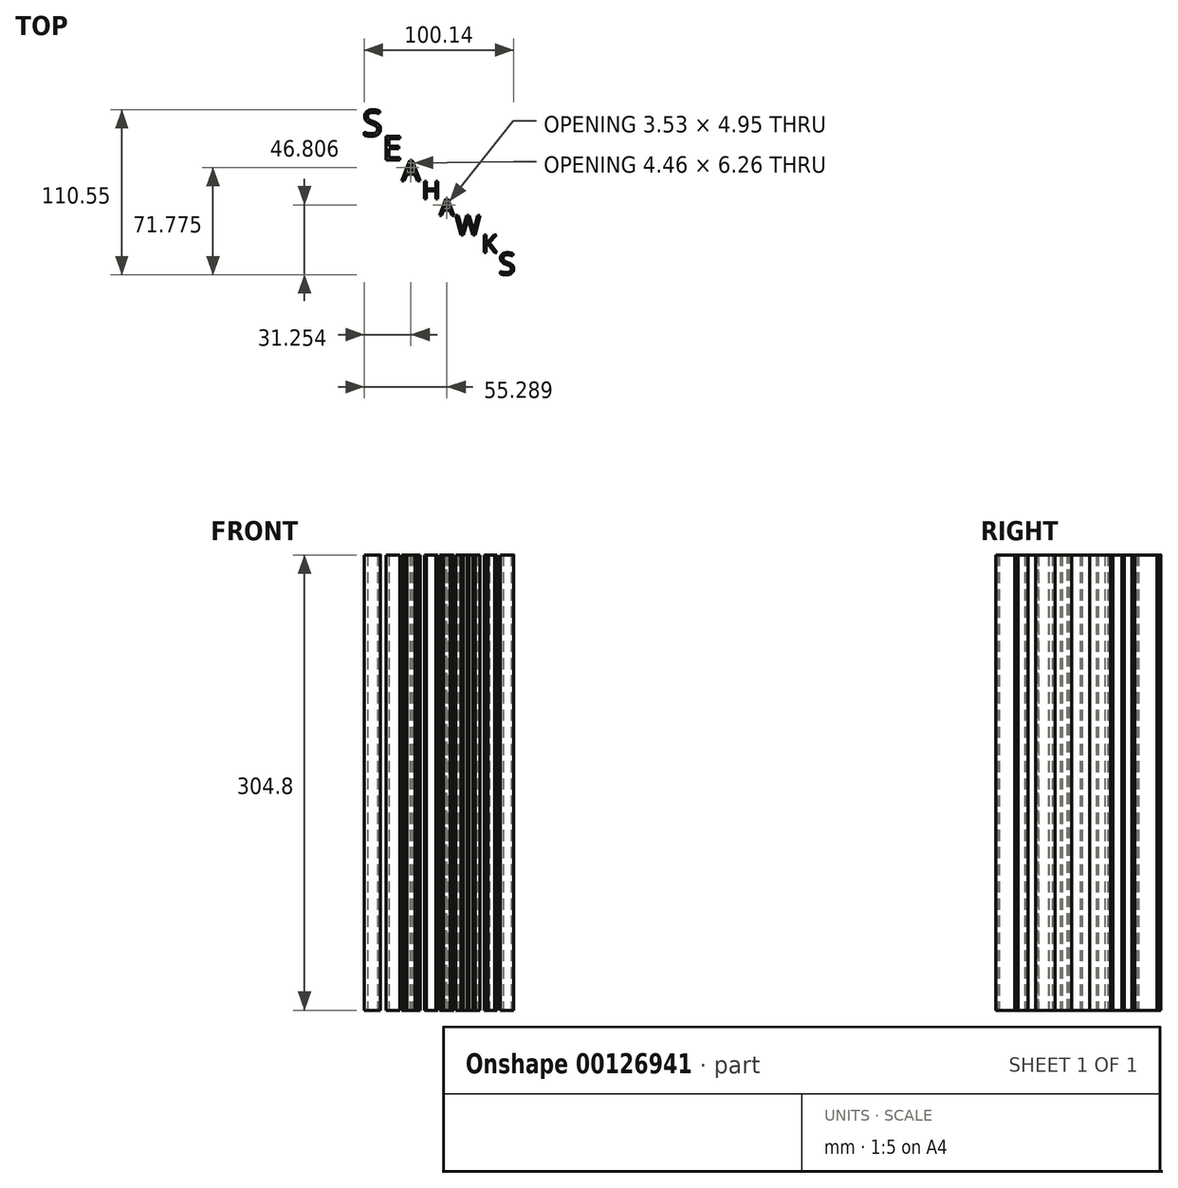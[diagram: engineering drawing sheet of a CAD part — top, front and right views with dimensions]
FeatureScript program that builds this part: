
annotation { "Feature Type Name" : "Feature", "Feature Type Description" : "" }
export const myFeature = defineFeature(function(context is Context, id is Id, definition is map)
    precondition{}
    {
        {
            var Q0;
            Q0=qCreatedBy(makeId("Top.planeOp"),FACE);
            var sketch = newSketch(context, id + "F0", { "sketchPlane" : qUnion([Q0])});
            skText(sketch, "E0", { "text": "S", "fontName": "OpenSans-Regular.ttf"});
            skText(sketch, "E1", { "text": "E", "fontName": "OpenSans-Regular.ttf"});
            skText(sketch, "E2", { "text": "A", "fontName": "OpenSans-Regular.ttf"});
            skText(sketch, "E3", { "text": "H", "fontName": "OpenSans-Regular.ttf"});
            skText(sketch, "E4", { "text": "A", "fontName": "OpenSans-Regular.ttf"});
            skText(sketch, "E5", { "text": "W", "fontName": "OpenSans-Regular.ttf"});
            skText(sketch, "E6", { "text": "K", "fontName": "OpenSans-Regular.ttf"});
            skText(sketch, "E7", { "text": "S", "fontName": "OpenSans-Regular.ttf"});
            const initialGuessF0  = {"E0": [-0.096, 0.07813, 1, 0, 0.0175], "E1": [-0.08224, 0.0619, 1, 0, 0.01624], "E2": [-0.0696, 0.048, 1, 0, 0.0139], "E3": [-0.05613, 0.0359, 1, 0, 0.01209], "E4": [-0.04429, 0.0249, 1, 0, 0.011], "E5": [-0.03362, 0.0119, 1, 0, 0.013], "E6": [-0.016, 0, 1, 0, 0.0119], "E7": [-0.00477, -0.01462, 1, 0, 0.01462]};
            skSetInitialGuess(sketch, initialGuessF0);
            skSolve(sketch);
        }
        {
            var Q0;
            Q0=makeQuery(id+"F0.imprint","IMPRINT",FACE,{"disambiguationData":[TD([[makeQuery(id+"F0.imprint","IMPRINT",EDGE,{"derivedFrom":sQuery(id+"F0.wireOp",EDGE,"E0.sketch_text.stroke-0")}),-1.0]])]});
            var Q1;
            Q1=makeQuery(id+"F0.imprint","IMPRINT",FACE,{"disambiguationData":[TD([[makeQuery(id+"F0.imprint","IMPRINT",EDGE,{"derivedFrom":sQuery(id+"F0.wireOp",EDGE,"E1.sketch_text.stroke-0")}),-1.0]])]});
            var Q2;
            Q2=makeQuery(id+"F0.imprint","IMPRINT",FACE,{"disambiguationData":[TD([[makeQuery(id+"F0.imprint","IMPRINT",EDGE,{"derivedFrom":sQuery(id+"F0.wireOp",EDGE,"E2.sketch_text.stroke-0")}),-1.0]])]});
            var Q3;
            Q3=makeQuery(id+"F0.imprint","IMPRINT",FACE,{"disambiguationData":[TD([[makeQuery(id+"F0.imprint","IMPRINT",EDGE,{"derivedFrom":sQuery(id+"F0.wireOp",EDGE,"E3.sketch_text.stroke-0")}),-1.0]])]});
            var Q4;
            Q4=makeQuery(id+"F0.imprint","IMPRINT",FACE,{"disambiguationData":[TD([[makeQuery(id+"F0.imprint","IMPRINT",EDGE,{"derivedFrom":sQuery(id+"F0.wireOp",EDGE,"E4.sketch_text.stroke-0")}),-1.0]])]});
            var Q5;
            Q5=makeQuery(id+"F0.imprint","IMPRINT",FACE,{"disambiguationData":[TD([[makeQuery(id+"F0.imprint","IMPRINT",EDGE,{"derivedFrom":sQuery(id+"F0.wireOp",EDGE,"E5.sketch_text.stroke-0")}),-1.0]])]});
            var Q6;
            Q6=makeQuery(id+"F0.imprint","IMPRINT",FACE,{"disambiguationData":[TD([[makeQuery(id+"F0.imprint","IMPRINT",EDGE,{"derivedFrom":sQuery(id+"F0.wireOp",EDGE,"E6.sketch_text.stroke-0")}),-1.0]])]});
            var Q7;
            Q7=makeQuery(id+"F0.imprint","IMPRINT",FACE,{"disambiguationData":[TD([[makeQuery(id+"F0.imprint","IMPRINT",EDGE,{"derivedFrom":sQuery(id+"F0.wireOp",EDGE,"E7.sketch_text.stroke-0")}),-1.0]])]});
            extrude(context, id + "F1", {"entities" : qUnion([Q0, Q1, Q2, Q3, Q4, Q5, Q6, Q7]), "depth" : 304.8 * mm});
        }
    });
